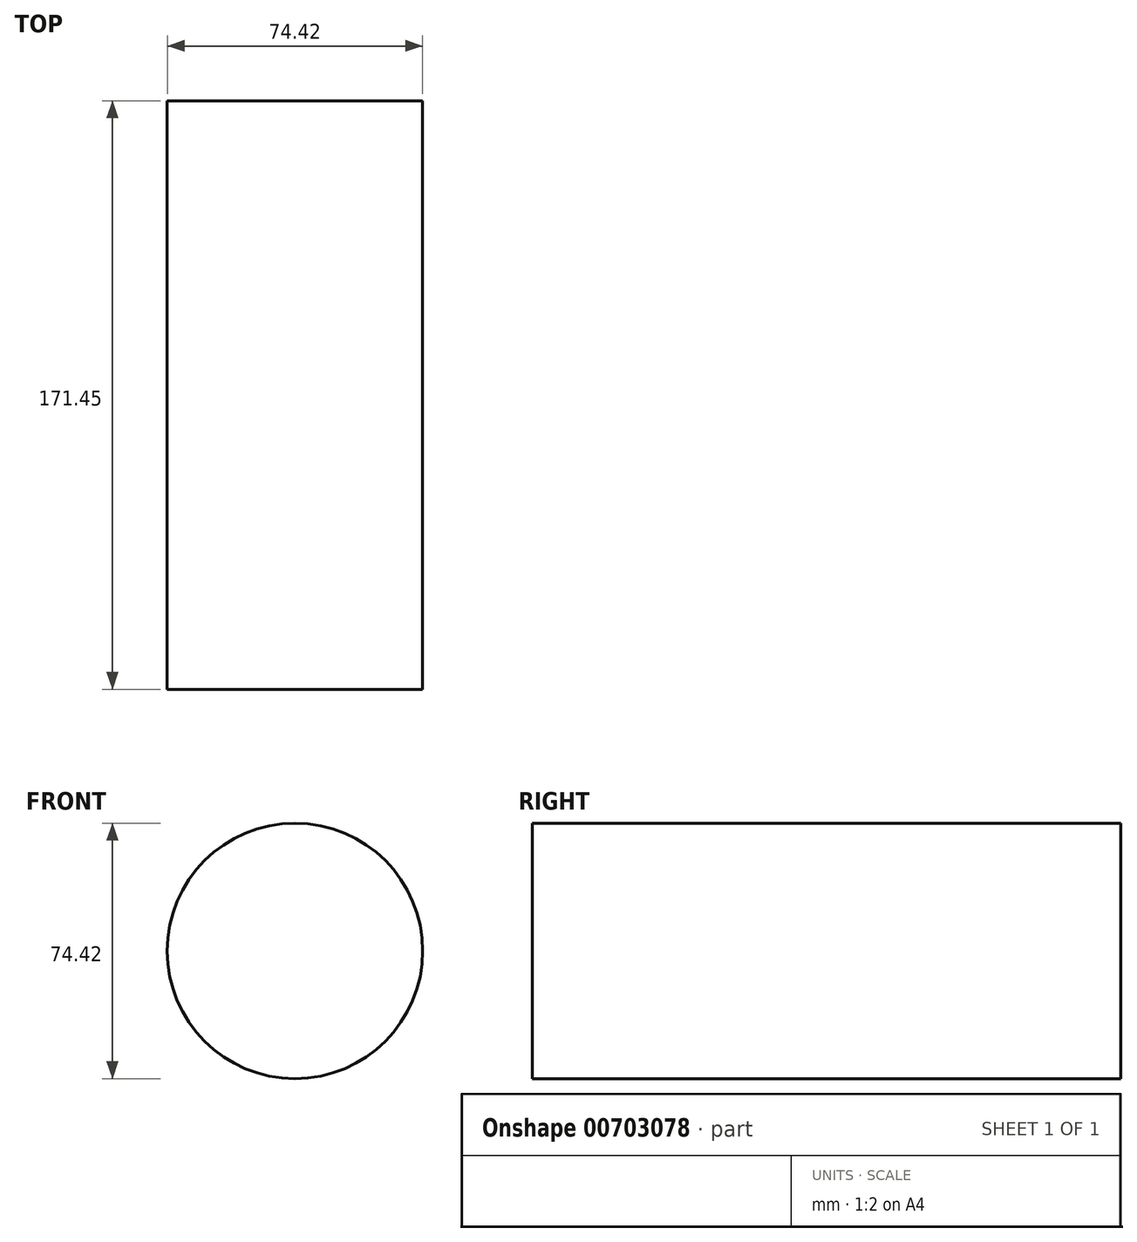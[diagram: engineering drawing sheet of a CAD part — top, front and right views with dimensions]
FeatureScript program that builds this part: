
annotation { "Feature Type Name" : "Feature", "Feature Type Description" : "" }
export const myFeature = defineFeature(function(context is Context, id is Id, definition is map)
    precondition{}
    {
        {
            var Q0;
            Q0=qCreatedBy(makeId("Front.planeOp"),FACE);
            var sketch = newSketch(context, id + "F0", { "sketchPlane" : qUnion([Q0])});
            skCircle(sketch, "E0", {"center": v(0, 0) * mm, "radius": 37.21 * mm});
            skSolve(sketch);
        }
        {
            var Q0;
            Q0=makeQuery(id+"F0.imprint","IMPRINT",FACE,{"disambiguationData":[TD([[makeQuery(id+"F0.imprint","IMPRINT",EDGE,{"derivedFrom":sQuery(id+"F0.wireOp",EDGE,"E0")}),1.0]])]});
            extrude(context, id + "F1", {"entities" : qUnion([Q0]), "depth" : 171.45 * mm, "offsetDistance" : 25.4 * mm});
        }
    });
